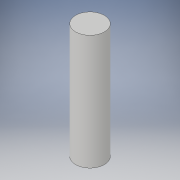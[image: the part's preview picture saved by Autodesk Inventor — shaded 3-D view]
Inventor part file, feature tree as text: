
AUTODESK INVENTOR PART (.ipt)
format: ipt  version: 2018.2 (Build 222227000, 227)  size: 90,112 bytes
history: native  units: in
note: dims shown in document units (in); Inventor stores cm internally (conversion verified against a paired STEP export)
features: extrude x1, sketch x1
ambient origin geometry x8: Origin, YZ Plane, XZ Plane, XY Plane, X Axis, Y Axis, Z Axis, Center Point
bodies: Solid1 (feature_tree)
feature tree (2):
  extrude  "Extrusion1"  Depth=4.0in TaperAngle=0.0deg
  sketch  "Sketch1"  dims[d0=1.0in d1=4.0in d2=0.0in]
